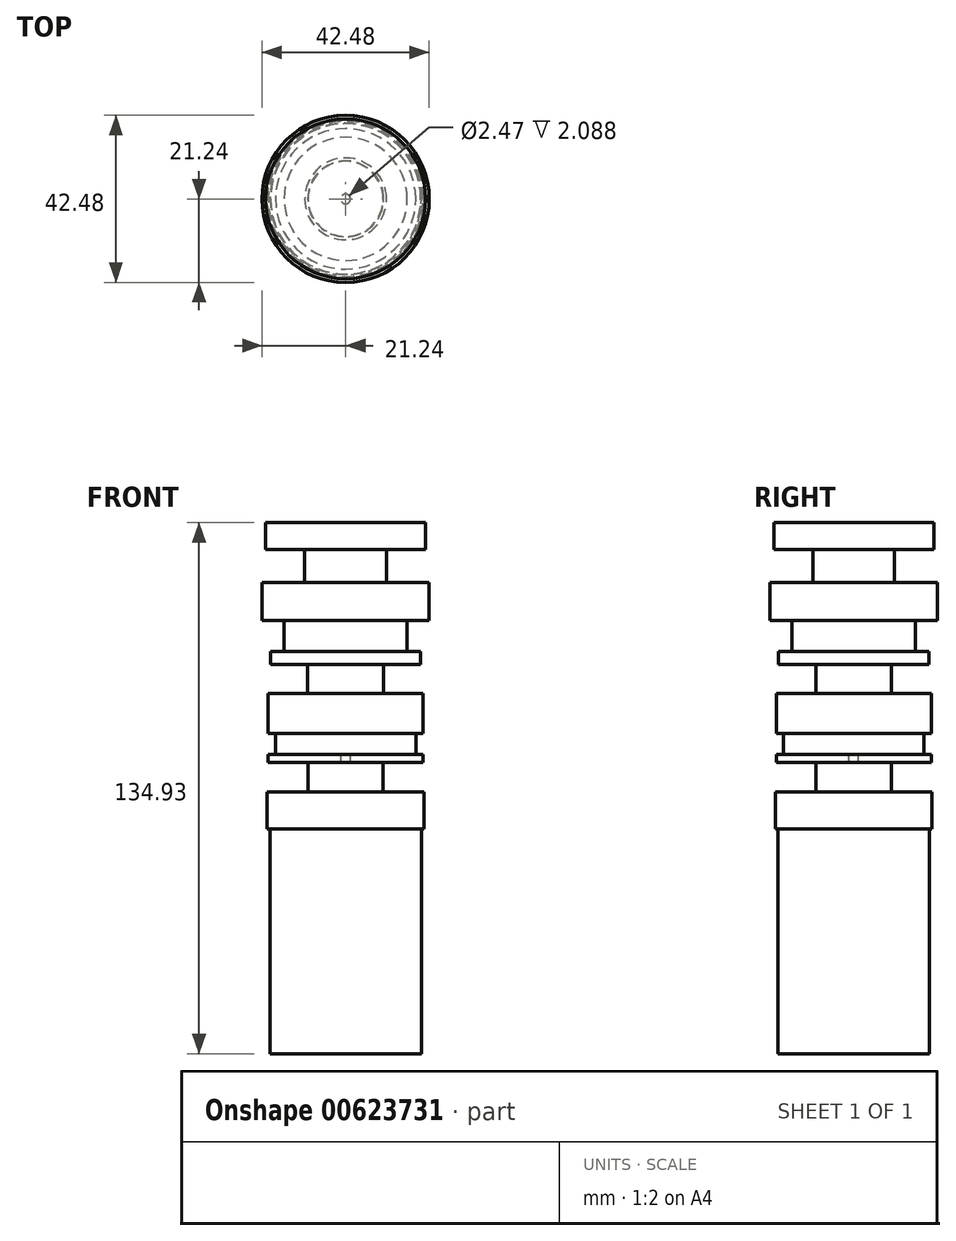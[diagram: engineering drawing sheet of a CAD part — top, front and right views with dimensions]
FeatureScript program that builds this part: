
annotation { "Feature Type Name" : "Feature", "Feature Type Description" : "" }
export const myFeature = defineFeature(function(context is Context, id is Id, definition is map)
    precondition{}
    {
        {
            var Q0;
            Q0=qCreatedBy(makeId("Front.planeOp"),FACE);
            var sketch = newSketch(context, id + "F0", { "sketchPlane" : qUnion([Q0])});
            skLineSegment(sketch, "E0.bottom", {"start": v(0, 60.94) * mm, "end": v(-20.31, 60.94) * mm});
            skLineSegment(sketch, "E0.top", {"start": v(0, 54.12) * mm, "end": v(-20.31, 54.12) * mm});
            skLineSegment(sketch, "E0.left", {"start": v(0, 60.94) * mm, "end": v(0, 54.12) * mm});
            skLineSegment(sketch, "E0.right", {"start": v(-20.31, 60.94) * mm, "end": v(-20.31, 54.12) * mm});
            skLineSegment(sketch, "E1.bottom", {"start": v(0, 54.12) * mm, "end": v(-10.39, 54.12) * mm});
            skLineSegment(sketch, "E1.top", {"start": v(0, 45.74) * mm, "end": v(-10.39, 45.74) * mm});
            skLineSegment(sketch, "E1.left", {"start": v(0, 54.12) * mm, "end": v(0, 45.74) * mm});
            skLineSegment(sketch, "E1.right", {"start": v(-10.39, 54.12) * mm, "end": v(-10.39, 45.74) * mm});
            skLineSegment(sketch, "E2.bottom", {"start": v(0, 45.74) * mm, "end": v(-21.24, 45.74) * mm});
            skLineSegment(sketch, "E2.top", {"start": v(0, 36.13) * mm, "end": v(-21.24, 36.13) * mm});
            skLineSegment(sketch, "E2.left", {"start": v(0, 45.74) * mm, "end": v(0, 36.13) * mm});
            skLineSegment(sketch, "E2.right", {"start": v(-21.24, 45.74) * mm, "end": v(-21.24, 36.13) * mm});
            skLineSegment(sketch, "E3.bottom", {"start": v(0, 36.13) * mm, "end": v(-15.64, 36.13) * mm});
            skLineSegment(sketch, "E3.top", {"start": v(0, 28.22) * mm, "end": v(-15.64, 28.22) * mm});
            skLineSegment(sketch, "E3.left", {"start": v(0, 36.13) * mm, "end": v(0, 28.22) * mm});
            skLineSegment(sketch, "E3.right", {"start": v(-15.64, 36.13) * mm, "end": v(-15.64, 28.22) * mm});
            skLineSegment(sketch, "E4.bottom", {"start": v(0, 28.22) * mm, "end": v(-19.08, 28.22) * mm});
            skLineSegment(sketch, "E4.top", {"start": v(0, 24.93) * mm, "end": v(-19.08, 24.93) * mm});
            skLineSegment(sketch, "E4.left", {"start": v(0, 28.22) * mm, "end": v(0, 24.93) * mm});
            skLineSegment(sketch, "E4.right", {"start": v(-19.08, 28.22) * mm, "end": v(-19.08, 24.93) * mm});
            skLineSegment(sketch, "E5.bottom", {"start": v(0, 24.93) * mm, "end": v(-9.64, 24.93) * mm});
            skLineSegment(sketch, "E5.top", {"start": v(0, 17.58) * mm, "end": v(-9.64, 17.58) * mm});
            skLineSegment(sketch, "E5.left", {"start": v(0, 24.93) * mm, "end": v(0, 17.58) * mm});
            skLineSegment(sketch, "E5.right", {"start": v(-9.64, 24.93) * mm, "end": v(-9.64, 17.58) * mm});
            skLineSegment(sketch, "E6.bottom", {"start": v(0, 17.58) * mm, "end": v(-19.68, 17.58) * mm});
            skLineSegment(sketch, "E6.top", {"start": v(0, 7.38) * mm, "end": v(-19.68, 7.38) * mm});
            skLineSegment(sketch, "E6.left", {"start": v(0, 17.58) * mm, "end": v(0, 7.38) * mm});
            skLineSegment(sketch, "E6.right", {"start": v(-19.68, 17.58) * mm, "end": v(-19.68, 7.38) * mm});
            skLineSegment(sketch, "E7.bottom", {"start": v(0, 7.38) * mm, "end": v(-17.83, 7.38) * mm});
            skLineSegment(sketch, "E7.top", {"start": v(0, 2.09) * mm, "end": v(-17.83, 2.09) * mm});
            skLineSegment(sketch, "E7.left", {"start": v(0, 7.38) * mm, "end": v(0, 2.09) * mm});
            skLineSegment(sketch, "E7.right", {"start": v(-17.83, 7.38) * mm, "end": v(-17.83, 2.09) * mm});
            skLineSegment(sketch, "E8.bottom", {"start": v(1.23, 2.09) * mm, "end": v(-19.68, 2.09) * mm});
            skLineSegment(sketch, "E8.top", {"start": v(1.23, 0) * mm, "end": v(-19.68, 0) * mm});
            skLineSegment(sketch, "E8.left", {"start": v(1.23, 2.09) * mm, "end": v(1.23, 0) * mm});
            skLineSegment(sketch, "E8.right", {"start": v(-19.68, 2.09) * mm, "end": v(-19.68, 0) * mm});
            skLineSegment(sketch, "E9.bottom", {"start": v(95.44, 0) * mm, "end": v(97.19, 0) * mm});
            skLineSegment(sketch, "E9.top", {"start": v(95.44, 7.38) * mm, "end": v(97.19, 7.38) * mm});
            skPoint(sketch, "E10.oppositeSnap0", {"position": v(-9.54, 28.22) * mm});
            skLineSegment(sketch, "E10.bottom", {"start": v(0, 0) * mm, "end": v(-9.54, 0) * mm});
            skLineSegment(sketch, "E10.top", {"start": v(0, -7.52) * mm, "end": v(-9.54, -7.52) * mm});
            skLineSegment(sketch, "E10.left", {"start": v(0, 0) * mm, "end": v(0, -7.52) * mm});
            skLineSegment(sketch, "E10.right", {"start": v(-9.54, 0) * mm, "end": v(-9.54, -7.52) * mm});
            skLineSegment(sketch, "E11.bottom", {"start": v(0, -7.52) * mm, "end": v(-19.9, -7.52) * mm});
            skLineSegment(sketch, "E11.top", {"start": v(0, -16.9) * mm, "end": v(-19.9, -16.9) * mm});
            skLineSegment(sketch, "E11.left", {"start": v(0, -7.52) * mm, "end": v(0, -16.9) * mm});
            skLineSegment(sketch, "E11.right", {"start": v(-19.9, -7.52) * mm, "end": v(-19.9, -16.9) * mm});
            skLineSegment(sketch, "E12.bottom", {"start": v(0, -16.9) * mm, "end": v(-19.24, -16.9) * mm});
            skLineSegment(sketch, "E12.top", {"start": v(0, -59.34) * mm, "end": v(-19.24, -59.34) * mm});
            skLineSegment(sketch, "E12.left", {"start": v(0, -16.9) * mm, "end": v(0, -59.34) * mm});
            skLineSegment(sketch, "E12.right", {"start": v(-19.24, -16.9) * mm, "end": v(-19.24, -59.34) * mm});
            skLineSegment(sketch, "E13.top", {"start": v(0, -74) * mm, "end": v(-19.24, -74) * mm});
            skLineSegment(sketch, "E13.left", {"start": v(0, -59.34) * mm, "end": v(0, -74) * mm});
            skLineSegment(sketch, "E13.right", {"start": v(-19.24, -59.34) * mm, "end": v(-19.24, -74) * mm});
            skSolve(sketch);
        }
        {
            var Q0;
            Q0 = qSketchRegion(id + "F0", true);
            var Q1;
            Q1=sQuery(id+"F0.wireOp",EDGE,"E12.left");
            revolve(context, id + "F1", {"entities" : qUnion([Q0]), "axis" : qUnion([Q1]), "revolveType" : RevolveType.FULL});
        }
    });
